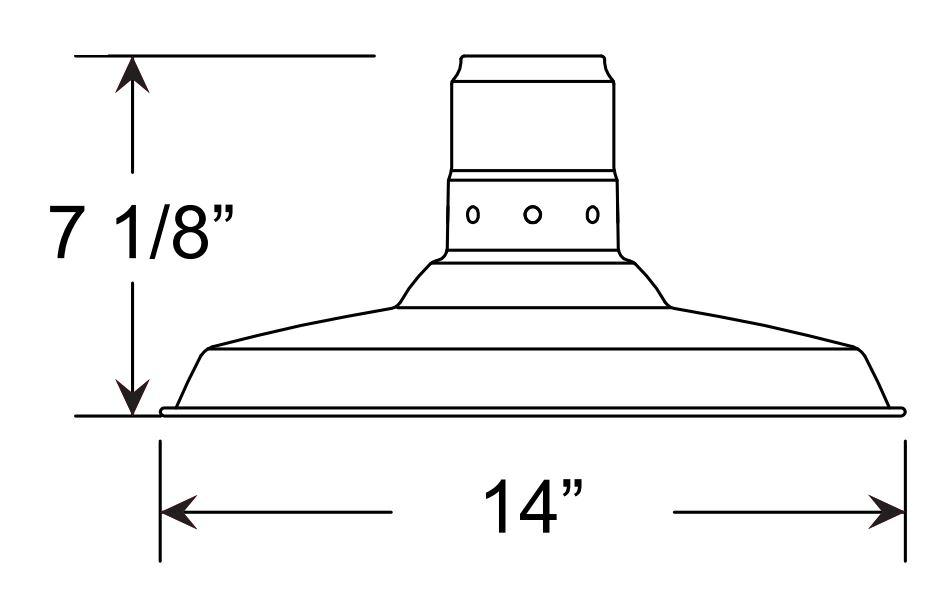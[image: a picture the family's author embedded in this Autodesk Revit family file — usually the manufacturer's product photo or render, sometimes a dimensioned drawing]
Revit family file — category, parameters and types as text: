
# Revit family: DEEP DOME_MB 12,16,20
name_source: partatom
category: Lighting Fixtures
units: mm (PartAtom-declared; Revit-internal decimal feet)

## family parameters
Always vertical = Yes
Cut with Voids When Loaded = No
Light Source = Yes
OmniClass Number = 23.80.70.00
OmniClass Title = Lighting
Part Type = Normal
Room Calculation Point = No
Round Connector Dimension = Use Diameter
Shared = No
Work Plane-Based = No

## types (3) — shared parameters
Apparent Load = 200 VA
Body Colour = Spun aluminium
Body Material = body
Bulb = Glass
CRI = >90
Canopy Body = body
Color Filter = 16777215
Construction Material = Heavy Duty spun aluminum.
Default Elevation = 0' - 0"
Description = 120-277 Voltage
Dimming = 1%
Dimming Lamp Color Temperature Shift = <None>
Efficiency = 97-125 lumens per watt
Lamp = MB
Life = L70 50,000 hours
Load Classification = Lighting
Manufacturer = ANP Lighting
Photometric Web File = generic
Power Factor = 1
Tilt Angle = 90.00°
URL = https://www.anplighting.com
Voltage = 120 V
Warranty = 5 year limited warranty
Wattage Comments = 200W

## per-type parameters (varying)
| type | DD12 | DD16 | DD20 | Fixture Diameter | Fixture Height | Weight | a | b |
| DD12 | Yes | No | No | 1' - 0" | 0' - 7 1/4" | 2.0 lb | 0' - 9 1/4" | 0' - 3" |
| DD16 | No | Yes | No | 1' - 4" | 0' - 9 3/4" | 4.0 lbs | 0' - 10 3/4" | 0' - 5 1/4" |
| DD20 | No | No | Yes | 1' - 8" | 1' - 0 1/4" | 6 lb | 1' - 0 1/4" | 0' - 7" |

note: column(s) folded — value = type name in every type: Model

## geometry (parser evidence)
native form markers: Sweep x49
no freeform markers — native parametric forms only
